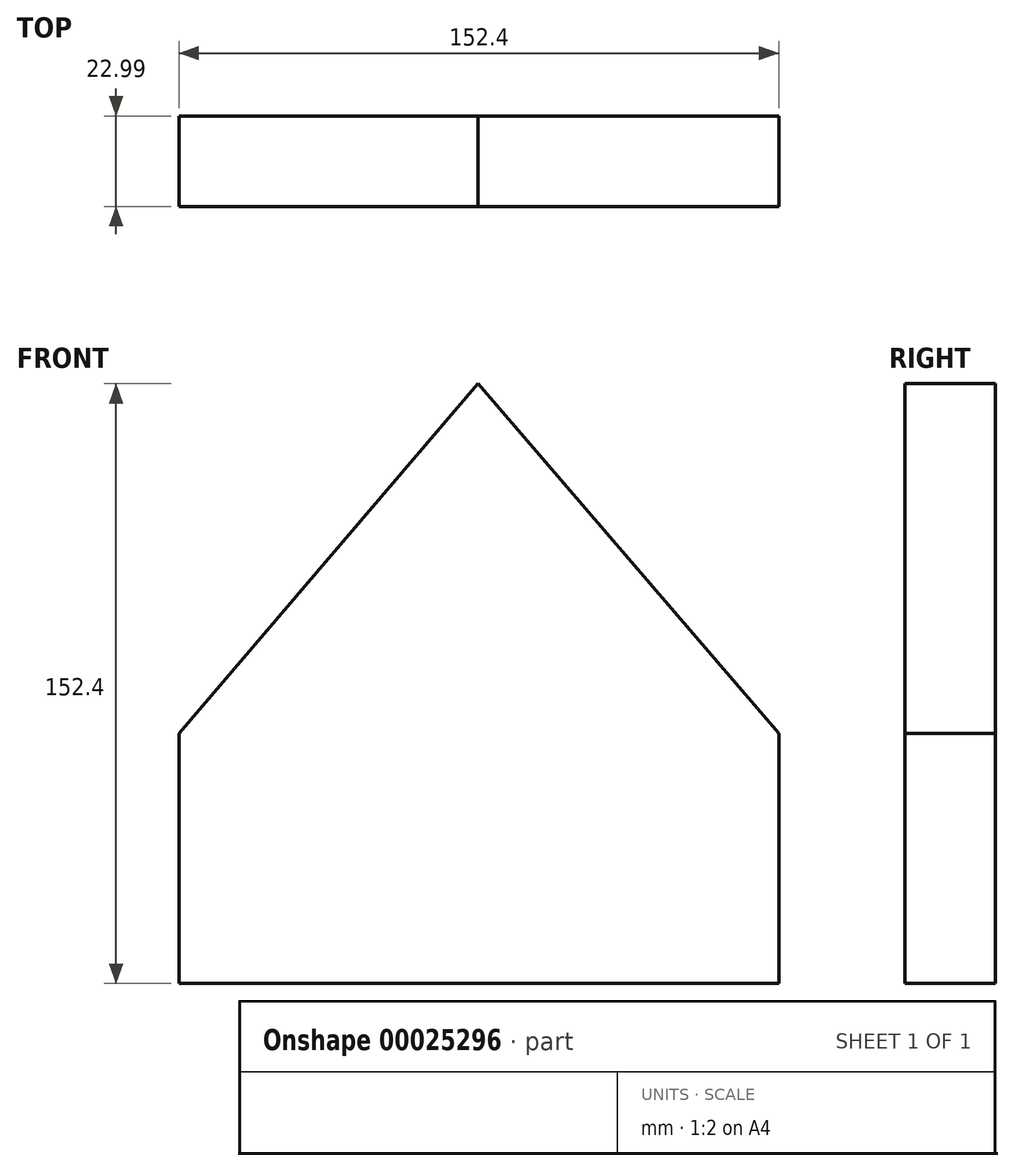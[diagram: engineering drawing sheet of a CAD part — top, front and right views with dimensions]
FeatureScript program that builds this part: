
annotation { "Feature Type Name" : "Feature", "Feature Type Description" : "" }
export const myFeature = defineFeature(function(context is Context, id is Id, definition is map)
    precondition{}
    {
        {
            var Q0;
            Q0=qCreatedBy(makeId("Front.planeOp"),FACE);
            var sketch = newSketch(context, id + "F0", { "sketchPlane" : qUnion([Q0])});
            skLineSegment(sketch, "E0", {"start": v(-75.92, 0) * mm, "end": v(-75.92, 63.5) * mm});
            skLineSegment(sketch, "E1", {"start": v(0, 152.4) * mm, "end": v(76.48, 63.5) * mm});
            skLineSegment(sketch, "E2", {"start": v(76.48, 63.5) * mm, "end": v(76.48, 0) * mm});
            skLineSegment(sketch, "E3", {"start": v(76.48, 0) * mm, "end": v(-75.92, 0) * mm});
            skLineSegment(sketch, "E4", {"start": v(0, 152.4) * mm, "end": v(-75.92, 63.5) * mm});
            skSolve(sketch);
        }
        {
            var Q0;
            Q0=makeQuery(id+"F0.imprint","IMPRINT",FACE,{"disambiguationData":[TD([[makeQuery(id+"F0.imprint","IMPRINT",EDGE,{"derivedFrom":sQuery(id+"F0.wireOp",EDGE,"E0")}),-1.0]])]});
            extrude(context, id + "F1", {"entities" : qUnion([Q0]), "depth" : 23 * mm});
        }
    });
